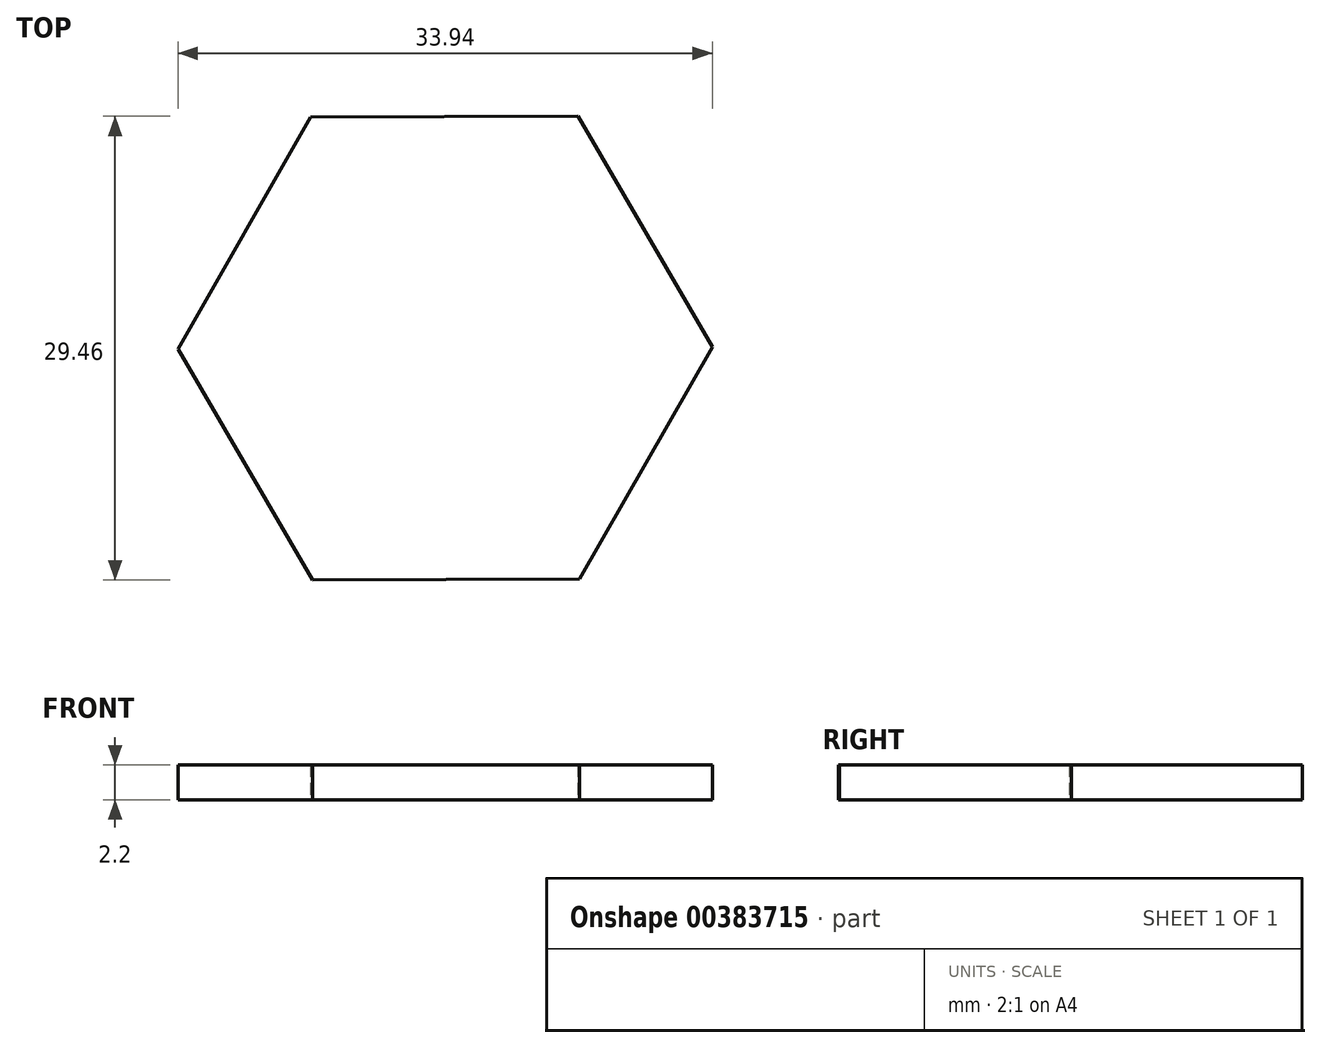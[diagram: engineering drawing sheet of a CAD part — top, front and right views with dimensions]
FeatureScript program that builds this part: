
annotation { "Feature Type Name" : "Feature", "Feature Type Description" : "" }
export const myFeature = defineFeature(function(context is Context, id is Id, definition is map)
    precondition{}
    {
        {
            var Q0;
            Q0=qCreatedBy(makeId("Top.planeOp"),FACE);
            var sketch = newSketch(context, id + "F0", { "sketchPlane" : qUnion([Q0])});
            skCircle(sketch, "E0.cCircle", {"center": v(0, 0) * mm, "radius": 14.7 * mm, "construction": true});
            skLineSegment(sketch, "E0.0", {"start": v(8.43, 14.73) * mm, "end": v(16.97, 0.07) * mm});
            skLineSegment(sketch, "E0.1", {"start": v(16.97, 0.07) * mm, "end": v(8.54, -14.67) * mm});
            skLineSegment(sketch, "E0.2", {"start": v(8.54, -14.67) * mm, "end": v(-8.43, -14.73) * mm});
            skLineSegment(sketch, "E0.3", {"start": v(-8.43, -14.73) * mm, "end": v(-16.97, -0.07) * mm});
            skLineSegment(sketch, "E0.4", {"start": v(-16.97, -0.07) * mm, "end": v(-8.54, 14.67) * mm});
            skLineSegment(sketch, "E0.5", {"start": v(-8.54, 14.67) * mm, "end": v(8.43, 14.73) * mm});
            skPoint(sketch, "E0.0.midPoint", {"position": v(12.7, 7.4) * mm});
            skSolve(sketch);
        }
        {
            var Q0;
            Q0=makeQuery(id+"F0.imprint","IMPRINT",FACE,{"disambiguationData":[TD([[makeQuery(id+"F0.imprint","IMPRINT",EDGE,{"derivedFrom":sQuery(id+"F0.wireOp",EDGE,"E0.0")}),-1.0]])]});
            extrude(context, id + "F1", {"entities" : qUnion([Q0]), "depth" : 2.2 * mm});
        }
    });
